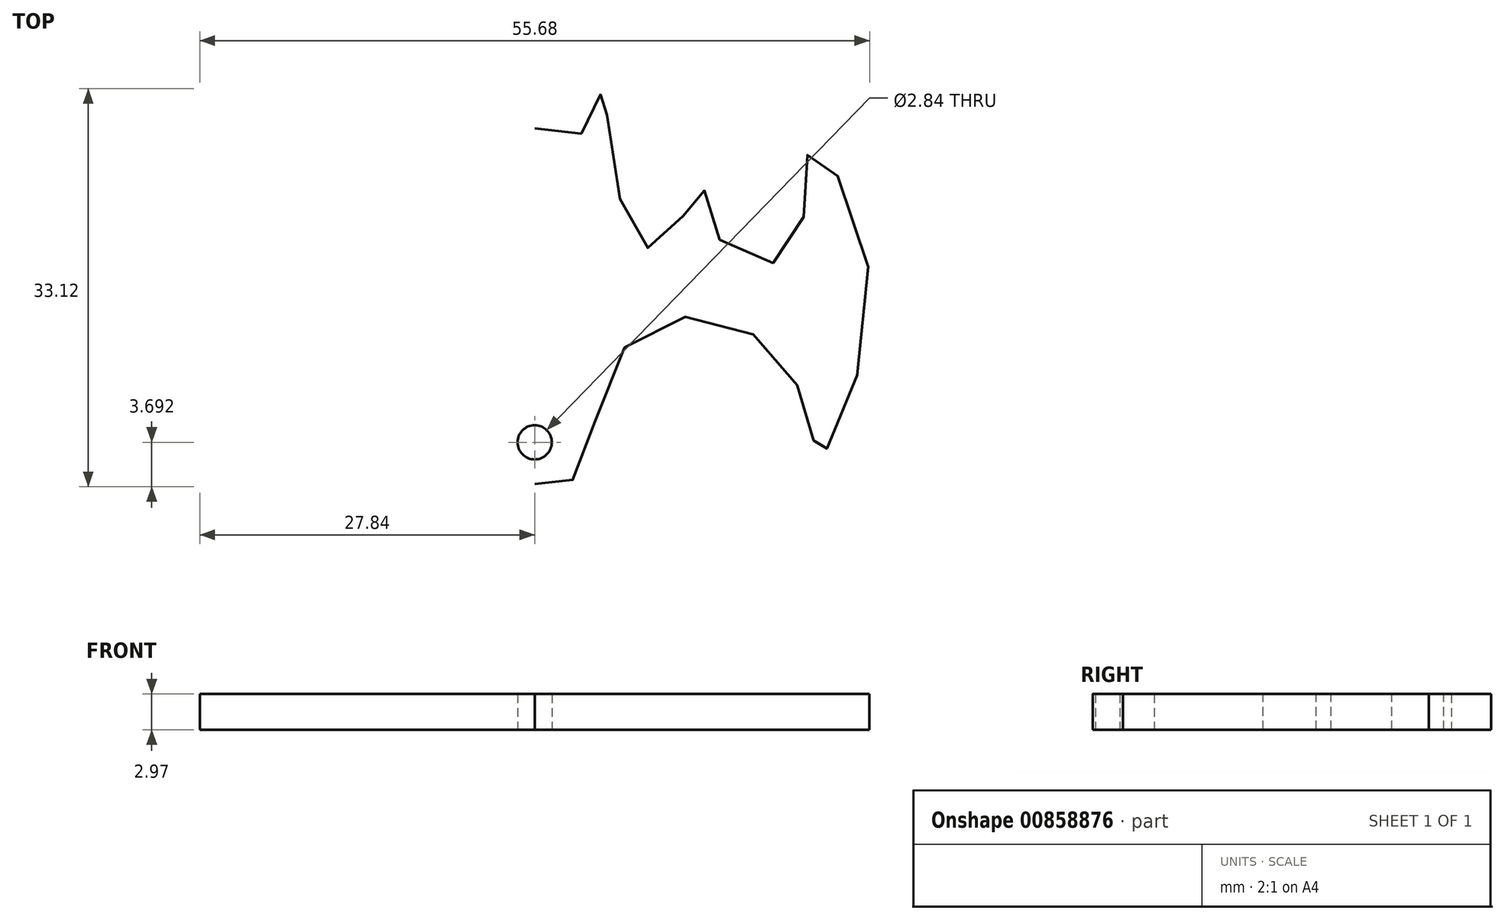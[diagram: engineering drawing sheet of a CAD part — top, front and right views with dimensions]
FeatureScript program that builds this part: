
annotation { "Feature Type Name" : "Feature", "Feature Type Description" : "" }
export const myFeature = defineFeature(function(context is Context, id is Id, definition is map)
    precondition{}
    {
        {
            var Q0;
            Q0=qCreatedBy(makeId("Top.planeOp"),FACE);
            var sketch = newSketch(context, id + "F0", { "sketchPlane" : qUnion([Q0])});
            skFitSpline(sketch, "E0", {"points": [v(0, 20.92) * mm, v(4.46, 20.92) * mm, v(5.62, 24.22) * mm, v(7.44, 13.8) * mm, v(10.42, 11.16) * mm, v(13.89, 15.96) * mm, v(15.38, 11.66) * mm, v(21.5, 10.67) * mm, v(22.82, 18.93) * mm, v(27.78, 8.85) * mm, v(23.65, -6.37) * mm, v(22.98, -3.72) * mm, v(17.7, 4.05) * mm, v(7.77, 3.06) * mm, v(3.3, -8.18) * mm, v(0, -8.68) * mm], "startDerivative": vector(99.61, -31.29) * mm, "endDerivative": vector(-80.17, 16.02) * mm});
            skFitSpline(sketch, "E1.MirrorCS", {"points": [v(0, 20.92) * mm, v(-4.46, 20.92) * mm, v(-5.62, 24.22) * mm, v(-7.44, 13.8) * mm, v(-10.42, 11.16) * mm, v(-13.89, 15.96) * mm, v(-15.38, 11.66) * mm, v(-21.5, 10.67) * mm, v(-22.82, 18.93) * mm, v(-27.78, 8.85) * mm, v(-23.65, -6.37) * mm, v(-22.98, -3.72) * mm, v(-17.7, 4.05) * mm, v(-7.77, 3.06) * mm, v(-3.3, -8.18) * mm, v(0, -8.68) * mm], "startDerivative": vector(-99.61, -31.29) * mm, "endDerivative": vector(80.17, 16.02) * mm});
            skCircle(sketch, "E2", {"center": v(0, -5.2) * mm, "radius": 1.42 * mm});
            skSolve(sketch);
        }
        {
            var Q0;
            Q0=makeQuery(id+"F0.imprint","IMPRINT",FACE,{"disambiguationData":[TD([[makeQuery(id+"F0.imprint","IMPRINT",EDGE,{"derivedFrom":sQuery(id+"F0.wireOp",EDGE,"E0")}),-1.0]])]});
            extrude(context, id + "F1", {"entities" : qUnion([Q0]), "depth" : 2.97 * mm, "offsetDistance" : 25.4 * mm});
        }
    });
